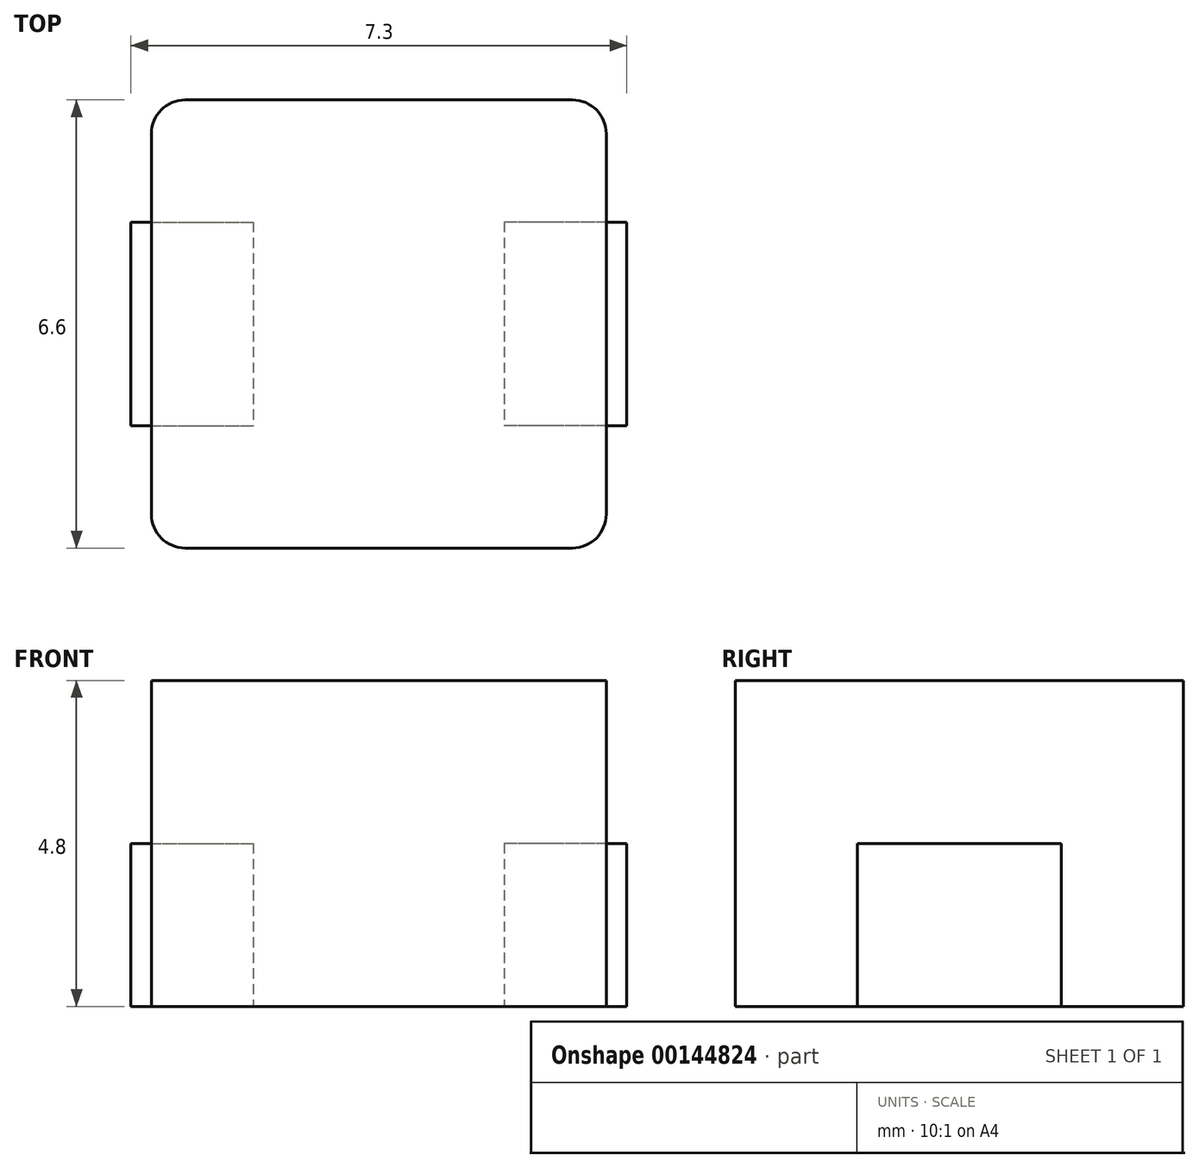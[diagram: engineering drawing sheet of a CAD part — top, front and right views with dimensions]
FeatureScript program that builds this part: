
annotation { "Feature Type Name" : "Feature", "Feature Type Description" : "" }
export const myFeature = defineFeature(function(context is Context, id is Id, definition is map)
    precondition{}
    {
        {
            var Q0;
            Q0=qCreatedBy(makeId("Top.planeOp"),FACE);
            var sketch = newSketch(context, id + "F0", { "sketchPlane" : qUnion([Q0])});
            skLineSegment(sketch, "E0.bottom", {"start": v(-3.65, 1.5) * mm, "end": v(-1.85, 1.5) * mm});
            skLineSegment(sketch, "E0.top", {"start": v(-3.65, -1.5) * mm, "end": v(-1.85, -1.5) * mm});
            skLineSegment(sketch, "E0.left", {"start": v(-3.65, 1.5) * mm, "end": v(-3.65, -1.5) * mm});
            skLineSegment(sketch, "E0.right", {"start": v(-1.85, 1.5) * mm, "end": v(-1.85, -1.5) * mm});
            skLineSegment(sketch, "E1.MirrorCS", {"start": v(3.65, 1.5) * mm, "end": v(1.85, 1.5) * mm});
            skLineSegment(sketch, "E2.MirrorCS", {"start": v(1.85, 1.5) * mm, "end": v(1.85, -1.5) * mm});
            skLineSegment(sketch, "E3.MirrorCS", {"start": v(3.65, -1.5) * mm, "end": v(1.85, -1.5) * mm});
            skLineSegment(sketch, "E4.MirrorCS", {"start": v(3.65, 1.5) * mm, "end": v(3.65, -1.5) * mm});
            skSolve(sketch);
        }
        {
            var Q0;
            Q0 = qSketchRegion(id + "F0", true);
            extrude(context, id + "F1", {"entities" : qUnion([Q0]), "depth" : 2.4 * mm});
        }
        {
            var Q0;
            Q0=qCreatedBy(makeId("Top.planeOp"),FACE);
            var sketch = newSketch(context, id + "F2", { "sketchPlane" : qUnion([Q0])});
            skLineSegment(sketch, "E5.bottom", {"start": v(-2.85, 3.3) * mm, "end": v(2.85, 3.3) * mm});
            skLineSegment(sketch, "E5.top", {"start": v(-2.85, -3.3) * mm, "end": v(2.85, -3.3) * mm});
            skLineSegment(sketch, "E5.left", {"start": v(-3.35, 2.8) * mm, "end": v(-3.35, -2.8) * mm});
            skLineSegment(sketch, "E5.right", {"start": v(3.35, 2.8) * mm, "end": v(3.35, -2.8) * mm});
            skPoint(sketch, "E6.visualSharp", {"position": v(-3.35, 3.3) * mm});
            skArc(sketch, "E6.filletArc", {"start": v(-2.85, 3.3) * mm, "mid": v(-3.2, 3.15) * mm, "end": v(-3.35, 2.8) * mm});
            skPoint(sketch, "E7.visualSharp", {"position": v(3.35, 3.3) * mm});
            skArc(sketch, "E7.filletArc", {"start": v(3.35, 2.8) * mm, "mid": v(3.2, 3.15) * mm, "end": v(2.85, 3.3) * mm});
            skPoint(sketch, "E8.visualSharp", {"position": v(3.35, -3.3) * mm});
            skArc(sketch, "E8.filletArc", {"start": v(2.85, -3.3) * mm, "mid": v(3.2, -3.15) * mm, "end": v(3.35, -2.8) * mm});
            skPoint(sketch, "E9.visualSharp", {"position": v(-3.35, -3.3) * mm});
            skArc(sketch, "E9.filletArc", {"start": v(-3.35, -2.8) * mm, "mid": v(-3.2, -3.15) * mm, "end": v(-2.85, -3.3) * mm});
            skSolve(sketch);
        }
        {
            var Q0;
            Q0 = qSketchRegion(id + "F2", true);
            extrude(context, id + "F3", {"entities" : qUnion([Q0]), "depth" : 4.8 * mm});
        }
    });
